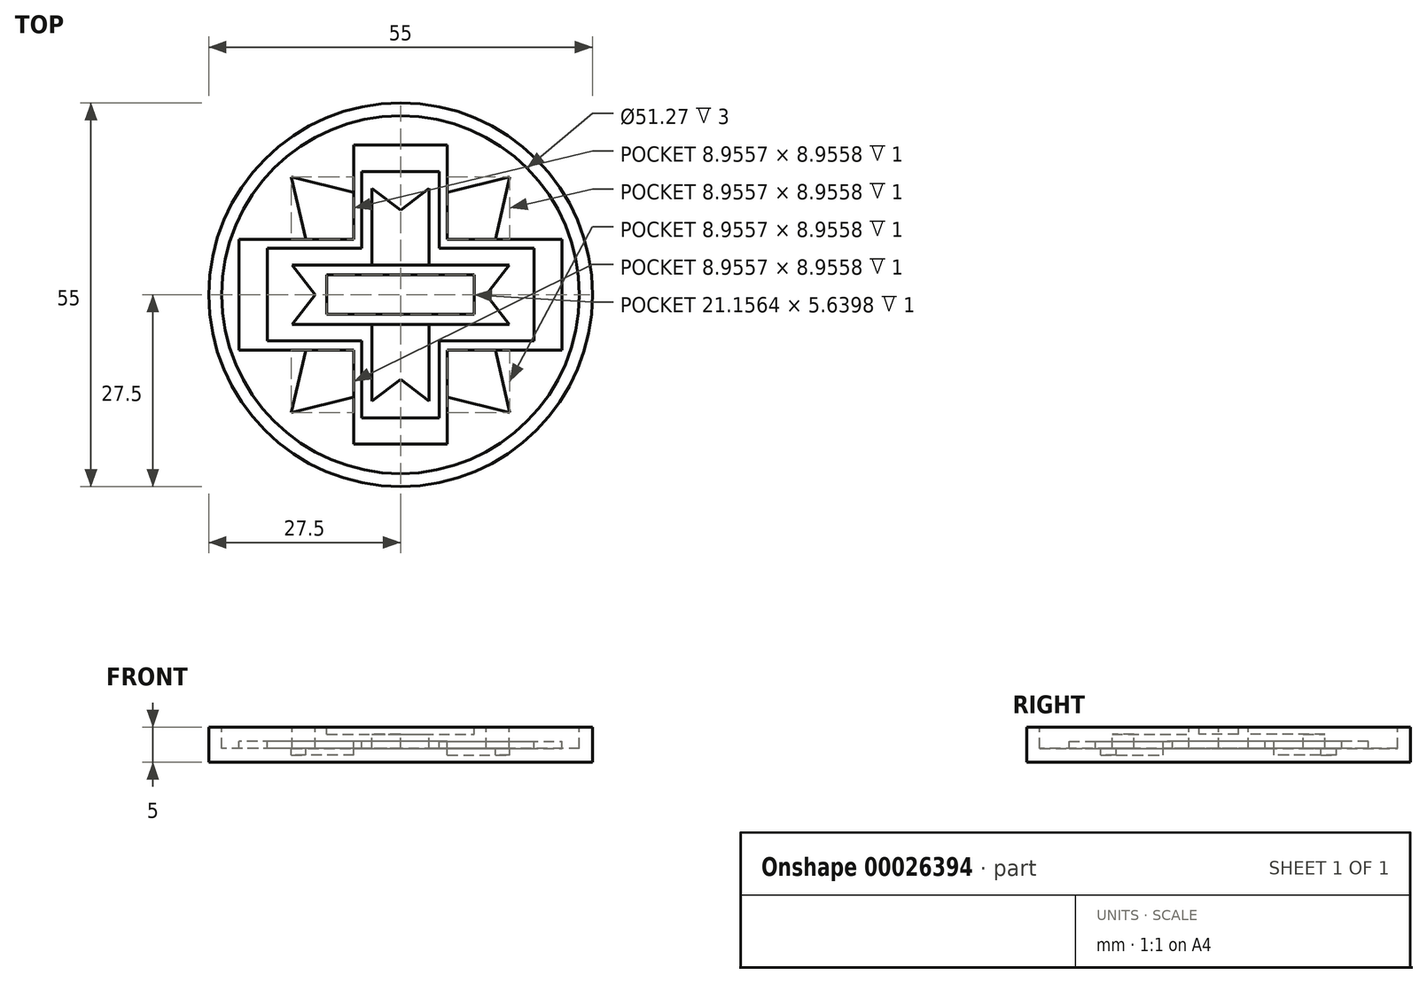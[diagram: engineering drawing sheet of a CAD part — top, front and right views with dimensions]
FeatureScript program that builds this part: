
annotation { "Feature Type Name" : "Feature", "Feature Type Description" : "" }
export const myFeature = defineFeature(function(context is Context, id is Id, definition is map)
    precondition{}
    {
        {
            var Q0;
            Q0=qCreatedBy(makeId("Top.planeOp"),FACE);
            var sketch = newSketch(context, id + "F0", { "sketchPlane" : qUnion([Q0])});
            skCircle(sketch, "E0", {"center": v(0, 0) * mm, "radius": 27.5 * mm});
            skCircle(sketch, "E1", {"center": v(0, 0) * mm, "radius": 25.64 * mm});
            skLineSegment(sketch, "E2", {"start": v(0, 2.82) * mm, "end": v(10.58, 2.82) * mm});
            skLineSegment(sketch, "E3", {"start": v(10.58, 2.82) * mm, "end": v(10.58, 0) * mm});
            skLineSegment(sketch, "E4", {"start": v(12.27, 0) * mm, "end": v(15.56, 4.28) * mm});
            skLineSegment(sketch, "E5", {"start": v(15.56, 4.28) * mm, "end": v(0, 4.28) * mm});
            skLineSegment(sketch, "E6", {"start": v(0, 12.14) * mm, "end": v(4.08, 15.25) * mm});
            skLineSegment(sketch, "E7", {"start": v(4.08, 15.25) * mm, "end": v(4.08, 4.28) * mm});
            skLineSegment(sketch, "E8", {"start": v(0, 17.64) * mm, "end": v(5.54, 17.64) * mm});
            skLineSegment(sketch, "E9", {"start": v(5.54, 17.64) * mm, "end": v(5.54, 6.63) * mm});
            skLineSegment(sketch, "E10", {"start": v(5.54, 6.63) * mm, "end": v(19.1, 6.63) * mm});
            skLineSegment(sketch, "E11", {"start": v(19.1, 6.63) * mm, "end": v(19.1, 0) * mm});
            skLineSegment(sketch, "E12", {"start": v(0, 21.43) * mm, "end": v(6.7, 21.43) * mm});
            skLineSegment(sketch, "E13", {"start": v(6.7, 21.43) * mm, "end": v(6.7, 7.94) * mm});
            skLineSegment(sketch, "E14", {"start": v(6.7, 7.94) * mm, "end": v(23.16, 7.94) * mm});
            skLineSegment(sketch, "E15", {"start": v(23.16, 7.94) * mm, "end": v(23.16, 0) * mm});
            skLineSegment(sketch, "E16", {"start": v(6.7, 14.69) * mm, "end": v(15.66, 16.9) * mm});
            skLineSegment(sketch, "E17", {"start": v(15.66, 16.9) * mm, "end": v(13.58, 7.94) * mm});
            skLineSegment(sketch, "E18", {"start": v(15.66, 16.9) * mm, "end": v(6.7, 7.94) * mm, "construction": true});
            skLineSegment(sketch, "E19.MirrorCS", {"start": v(0, 21.43) * mm, "end": v(-6.7, 21.43) * mm});
            skLineSegment(sketch, "E20.MirrorCS", {"start": v(0, 17.64) * mm, "end": v(-5.54, 17.64) * mm});
            skLineSegment(sketch, "E21.MirrorCS", {"start": v(0, 12.14) * mm, "end": v(-4.08, 15.25) * mm});
            skLineSegment(sketch, "E22.MirrorCS", {"start": v(-15.56, 4.28) * mm, "end": v(0, 4.28) * mm});
            skLineSegment(sketch, "E23.MirrorCS", {"start": v(0, 2.82) * mm, "end": v(-10.58, 2.82) * mm});
            skLineSegment(sketch, "E24.MirrorCS", {"start": v(-4.08, 15.25) * mm, "end": v(-4.08, 4.28) * mm});
            skLineSegment(sketch, "E25.MirrorCS", {"start": v(-12.27, 0) * mm, "end": v(-15.56, 4.28) * mm});
            skLineSegment(sketch, "E26.MirrorCS", {"start": v(-10.58, 2.82) * mm, "end": v(-10.58, 0) * mm});
            skLineSegment(sketch, "E27.MirrorCS", {"start": v(-19.1, 6.63) * mm, "end": v(-19.1, 0) * mm});
            skLineSegment(sketch, "E28.MirrorCS", {"start": v(-6.7, 7.94) * mm, "end": v(-23.16, 7.94) * mm});
            skLineSegment(sketch, "E29.MirrorCS", {"start": v(-6.7, 21.43) * mm, "end": v(-6.7, 7.94) * mm});
            skLineSegment(sketch, "E30.MirrorCS", {"start": v(-5.54, 17.64) * mm, "end": v(-5.54, 6.63) * mm});
            skLineSegment(sketch, "E31.MirrorCS", {"start": v(-5.54, 6.63) * mm, "end": v(-19.1, 6.63) * mm});
            skLineSegment(sketch, "E32.MirrorCS", {"start": v(-23.16, 7.94) * mm, "end": v(-23.16, 0) * mm});
            skLineSegment(sketch, "E33.MirrorCS", {"start": v(-15.66, 16.9) * mm, "end": v(-13.58, 7.94) * mm});
            skLineSegment(sketch, "E34.MirrorCS", {"start": v(-6.7, 14.69) * mm, "end": v(-15.66, 16.9) * mm});
            skLineSegment(sketch, "E35.MirrorCS", {"start": v(-10.58, -2.82) * mm, "end": v(-10.58, 0) * mm});
            skLineSegment(sketch, "E36.MirrorCS", {"start": v(0, -2.82) * mm, "end": v(-10.58, -2.82) * mm});
            skLineSegment(sketch, "E37.MirrorCS", {"start": v(0, -2.82) * mm, "end": v(10.58, -2.82) * mm});
            skLineSegment(sketch, "E38.MirrorCS", {"start": v(10.58, -2.82) * mm, "end": v(10.58, 0) * mm});
            skLineSegment(sketch, "E39.MirrorCS", {"start": v(12.27, 0) * mm, "end": v(15.56, -4.28) * mm});
            skLineSegment(sketch, "E40.MirrorCS", {"start": v(15.56, -4.28) * mm, "end": v(0, -4.28) * mm});
            skLineSegment(sketch, "E41.MirrorCS", {"start": v(-15.56, -4.28) * mm, "end": v(0, -4.28) * mm});
            skLineSegment(sketch, "E42.MirrorCS", {"start": v(-12.27, 0) * mm, "end": v(-15.56, -4.28) * mm});
            skLineSegment(sketch, "E43.MirrorCS", {"start": v(-4.08, -15.25) * mm, "end": v(-4.08, -4.28) * mm});
            skLineSegment(sketch, "E44.MirrorCS", {"start": v(0, -12.14) * mm, "end": v(-4.08, -15.25) * mm});
            skLineSegment(sketch, "E45.MirrorCS", {"start": v(0, -12.14) * mm, "end": v(4.08, -15.25) * mm});
            skLineSegment(sketch, "E46.MirrorCS", {"start": v(4.08, -15.25) * mm, "end": v(4.08, -4.28) * mm});
            skLineSegment(sketch, "E47.MirrorCS", {"start": v(-19.1, -6.63) * mm, "end": v(-19.1, 0) * mm});
            skLineSegment(sketch, "E48.MirrorCS", {"start": v(-5.54, -6.63) * mm, "end": v(-19.1, -6.63) * mm});
            skLineSegment(sketch, "E49.MirrorCS", {"start": v(-5.54, -17.64) * mm, "end": v(-5.54, -6.63) * mm});
            skLineSegment(sketch, "E50.MirrorCS", {"start": v(0, -17.64) * mm, "end": v(-5.54, -17.64) * mm});
            skLineSegment(sketch, "E51.MirrorCS", {"start": v(0, -17.64) * mm, "end": v(5.54, -17.64) * mm});
            skLineSegment(sketch, "E52.MirrorCS", {"start": v(5.54, -17.64) * mm, "end": v(5.54, -6.63) * mm});
            skLineSegment(sketch, "E53.MirrorCS", {"start": v(5.54, -6.63) * mm, "end": v(19.1, -6.63) * mm});
            skLineSegment(sketch, "E54.MirrorCS", {"start": v(19.1, -6.63) * mm, "end": v(19.1, 0) * mm});
            skLineSegment(sketch, "E55.MirrorCS", {"start": v(23.16, -7.94) * mm, "end": v(23.16, 0) * mm});
            skLineSegment(sketch, "E56.MirrorCS", {"start": v(6.7, -7.94) * mm, "end": v(23.16, -7.94) * mm});
            skLineSegment(sketch, "E57.MirrorCS", {"start": v(6.7, -21.43) * mm, "end": v(6.7, -7.94) * mm});
            skLineSegment(sketch, "E58.MirrorCS", {"start": v(6.7, -14.69) * mm, "end": v(15.66, -16.9) * mm});
            skLineSegment(sketch, "E59.MirrorCS", {"start": v(15.66, -16.9) * mm, "end": v(13.58, -7.94) * mm});
            skLineSegment(sketch, "E60.MirrorCS", {"start": v(0, -21.43) * mm, "end": v(6.7, -21.43) * mm});
            skLineSegment(sketch, "E61.MirrorCS", {"start": v(0, -21.43) * mm, "end": v(-6.7, -21.43) * mm});
            skLineSegment(sketch, "E62.MirrorCS", {"start": v(-6.7, -21.43) * mm, "end": v(-6.7, -7.94) * mm});
            skLineSegment(sketch, "E63.MirrorCS", {"start": v(-6.7, -14.69) * mm, "end": v(-15.66, -16.9) * mm});
            skLineSegment(sketch, "E64.MirrorCS", {"start": v(-15.66, -16.9) * mm, "end": v(-13.58, -7.94) * mm});
            skLineSegment(sketch, "E65.MirrorCS", {"start": v(-6.7, -7.94) * mm, "end": v(-23.16, -7.94) * mm});
            skLineSegment(sketch, "E66.MirrorCS", {"start": v(-23.16, -7.94) * mm, "end": v(-23.16, 0) * mm});
            skSolve(sketch);
        }
        {
            var Q0;
            Q0=makeQuery(id+"F0.imprint","IMPRINT",FACE,{"disambiguationData":[TD([[makeQuery(id+"F0.imprint","IMPRINT",EDGE,{"derivedFrom":sQuery(id+"F0.wireOp",EDGE,"E0")}),1.0]])]});
            var Q1;
            Q1=makeQuery(id+"F0.imprint","IMPRINT",FACE,{"disambiguationData":[TD([[makeQuery(id+"F0.imprint","IMPRINT",EDGE,{"derivedFrom":sQuery(id+"F0.wireOp",EDGE,"E1")}),1.0]])]});
            var Q2;
            Q2=makeQuery(id+"F0.imprint","IMPRINT",FACE,{"disambiguationData":[TD([[makeQuery(id+"F0.imprint","IMPRINT",EDGE,{"derivedFrom":sQuery(id+"F0.wireOp",EDGE,"E8")}),1.0]])]});
            var Q3;
            {var subQ3=sQuery(id+"F0.wireOp",EDGE,"E33.MirrorCS");Q3=makeQuery(id+"F0.imprint","IMPRINT",FACE,{"disambiguationData":[TD([[makeQuery(id+"F0.imprint","IMPRINT",EDGE,{"derivedFrom":subQ3}),1.0]])]});}
            var Q4;
            {var subQ7=sQuery(id+"F0.wireOp",EDGE,"E4");Q4=makeQuery(id+"F0.imprint","IMPRINT",FACE,{"disambiguationData":[TD([[makeQuery(id+"F0.imprint","IMPRINT",EDGE,{"derivedFrom":subQ7}),-1.0]])]});}
            var Q5;
            Q5=makeQuery(id+"F0.imprint","IMPRINT",FACE,{"disambiguationData":[TD([[makeQuery(id+"F0.imprint","IMPRINT",EDGE,{"derivedFrom":sQuery(id+"F0.wireOp",EDGE,"E6")}),-1.0]])]});
            var Q6;
            Q6=makeQuery(id+"F0.imprint","IMPRINT",FACE,{"disambiguationData":[TD([[makeQuery(id+"F0.imprint","IMPRINT",EDGE,{"derivedFrom":sQuery(id+"F0.wireOp",EDGE,"E2")}),-1.0]])]});
            var Q7;
            Q7=makeQuery(id+"F0.imprint","IMPRINT",FACE,{"disambiguationData":[TD([[makeQuery(id+"F0.imprint","IMPRINT",EDGE,{"derivedFrom":sQuery(id+"F0.wireOp",EDGE,"E2")}),1.0]])]});
            var Q8;
            {var subQ4=sQuery(id+"F0.wireOp",EDGE,"E58.MirrorCS");Q8=makeQuery(id+"F0.imprint","IMPRINT",FACE,{"disambiguationData":[TD([[makeQuery(id+"F0.imprint","IMPRINT",EDGE,{"derivedFrom":subQ4}),1.0]])]});}
            var Q9;
            {var subQ0=sQuery(id+"F0.wireOp",EDGE,"E43.MirrorCS");Q9=makeQuery(id+"F0.imprint","IMPRINT",FACE,{"disambiguationData":[TD([[makeQuery(id+"F0.imprint","IMPRINT",EDGE,{"derivedFrom":subQ0}),-1.0]])]});}
            var Q10;
            {var subQ3=sQuery(id+"F0.wireOp",EDGE,"E63.MirrorCS");Q10=makeQuery(id+"F0.imprint","IMPRINT",FACE,{"disambiguationData":[TD([[makeQuery(id+"F0.imprint","IMPRINT",EDGE,{"derivedFrom":subQ3}),-1.0]])]});}
            var Q11;
            {var subQ3=sQuery(id+"F0.wireOp",EDGE,"E16");Q11=makeQuery(id+"F0.imprint","IMPRINT",FACE,{"disambiguationData":[TD([[makeQuery(id+"F0.imprint","IMPRINT",EDGE,{"derivedFrom":subQ3}),-1.0]])]});}
            extrude(context, id + "F1", {"entities" : qUnion([Q0, Q1, Q2, Q3, Q4, Q5, Q6, Q7, Q8, Q9, Q10, Q11]), "oppositeDirection" : true, "depth" : 5 * mm});
        }
        {
            var Q0;
            Q0=makeQuery(id+"F0.imprint","IMPRINT",FACE,{"disambiguationData":[TD([[makeQuery(id+"F0.imprint","IMPRINT",EDGE,{"derivedFrom":sQuery(id+"F0.wireOp",EDGE,"E1")}),1.0]])]});
            extrude(context, id + "F2", {"entities" : qUnion([Q0]), "operationType" : NewBodyOperationType.REMOVE, "oppositeDirection" : true, "depth" : 3 * mm});
        }
        {
            var Q0;
            {var subQ3=sQuery(id+"F0.wireOp",EDGE,"E33.MirrorCS");Q0=makeQuery(id+"F0.imprint","IMPRINT",FACE,{"disambiguationData":[TD([[makeQuery(id+"F0.imprint","IMPRINT",EDGE,{"derivedFrom":subQ3}),1.0]])]});}
            var Q1;
            {var subQ3=sQuery(id+"F0.wireOp",EDGE,"E16");Q1=makeQuery(id+"F0.imprint","IMPRINT",FACE,{"disambiguationData":[TD([[makeQuery(id+"F0.imprint","IMPRINT",EDGE,{"derivedFrom":subQ3}),-1.0]])]});}
            var Q2;
            {var subQ4=sQuery(id+"F0.wireOp",EDGE,"E58.MirrorCS");Q2=makeQuery(id+"F0.imprint","IMPRINT",FACE,{"disambiguationData":[TD([[makeQuery(id+"F0.imprint","IMPRINT",EDGE,{"derivedFrom":subQ4}),1.0]])]});}
            var Q3;
            {var subQ3=sQuery(id+"F0.wireOp",EDGE,"E63.MirrorCS");Q3=makeQuery(id+"F0.imprint","IMPRINT",FACE,{"disambiguationData":[TD([[makeQuery(id+"F0.imprint","IMPRINT",EDGE,{"derivedFrom":subQ3}),-1.0]])]});}
            extrude(context, id + "F3", {"entities" : qUnion([Q0, Q1, Q2, Q3]), "operationType" : NewBodyOperationType.REMOVE, "oppositeDirection" : true, "depth" : 4 * mm});
        }
        {
            var Q0;
            Q0=makeQuery(id+"F0.imprint","IMPRINT",FACE,{"disambiguationData":[TD([[makeQuery(id+"F0.imprint","IMPRINT",EDGE,{"derivedFrom":sQuery(id+"F0.wireOp",EDGE,"E8")}),1.0]])]});
            extrude(context, id + "F4", {"entities" : qUnion([Q0]), "operationType" : NewBodyOperationType.REMOVE, "oppositeDirection" : true, "depth" : 2 * mm});
        }
        {
            var Q0;
            {var subQ7=sQuery(id+"F0.wireOp",EDGE,"E4");Q0=makeQuery(id+"F0.imprint","IMPRINT",FACE,{"disambiguationData":[TD([[makeQuery(id+"F0.imprint","IMPRINT",EDGE,{"derivedFrom":subQ7}),-1.0]])]});}
            extrude(context, id + "F5", {"entities" : qUnion([Q0]), "operationType" : NewBodyOperationType.REMOVE, "oppositeDirection" : true, "depth" : 3 * mm});
        }
        {
            var Q0;
            Q0=makeQuery(id+"F0.imprint","IMPRINT",FACE,{"disambiguationData":[TD([[makeQuery(id+"F0.imprint","IMPRINT",EDGE,{"derivedFrom":sQuery(id+"F0.wireOp",EDGE,"E6")}),-1.0]])]});
            var Q1;
            {var subQ0=sQuery(id+"F0.wireOp",EDGE,"E43.MirrorCS");Q1=makeQuery(id+"F0.imprint","IMPRINT",FACE,{"disambiguationData":[TD([[makeQuery(id+"F0.imprint","IMPRINT",EDGE,{"derivedFrom":subQ0}),-1.0]])]});}
            extrude(context, id + "F6", {"entities" : qUnion([Q0, Q1]), "operationType" : NewBodyOperationType.REMOVE, "oppositeDirection" : true, "depth" : 1 * mm});
        }
        {
            var Q0;
            Q0=makeQuery(id+"F0.imprint","IMPRINT",FACE,{"disambiguationData":[TD([[makeQuery(id+"F0.imprint","IMPRINT",EDGE,{"derivedFrom":sQuery(id+"F0.wireOp",EDGE,"E2")}),-1.0]])]});
            extrude(context, id + "F7", {"entities" : qUnion([Q0]), "operationType" : NewBodyOperationType.REMOVE, "oppositeDirection" : true, "depth" : 1 * mm});
        }
    });
